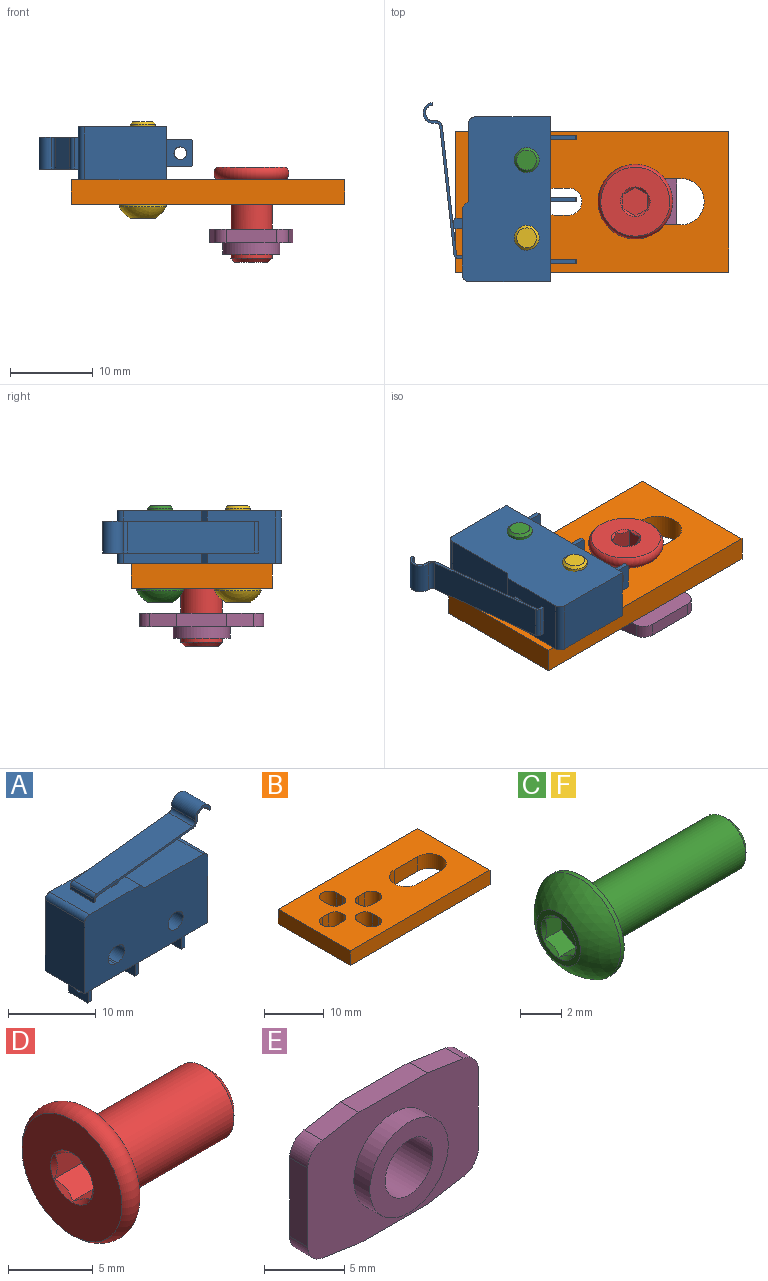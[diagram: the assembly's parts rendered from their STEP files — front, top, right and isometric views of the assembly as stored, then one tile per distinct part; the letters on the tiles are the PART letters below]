
ASSEMBLY  parts=6 mates=5
PART A: 58 faces, bbox 21.6x6.4x18.6 mm
  f0: cylinder r=0.76mm len=1.52mm, axis (-1,0,0), area 2.4mm2, adj f51,f52
  f1: cylinder r=0.76mm len=1.52mm, axis (-1,0,0), area 2.4mm2, adj f44,f45
  f2: cylinder r=0.76mm len=1.52mm, axis (-1,0,0), area 2.4mm2, adj f37,f38
  f3: cylinder r=1.21mm len=6.35mm, axis (0,1,0), area 24.1mm2, adj f26,f27,f34,f36
  f4: cylinder r=1.21mm len=6.35mm, axis (0,1,0), area 48.1mm2, adj f26,f27
  f5: cylinder r=1.27mm len=3.81mm, axis (0,1,0), area 15.2mm2, adj f14,f15,f22,f23
  f6: cylinder r=0.97mm len=3.81mm, axis (0,1,0), area 11.6mm2, adj f14,f21,f22,f23
  f7: cylinder r=1.02mm len=2.21mm, axis (0,1,0), area 1.4mm2, adj f9,f10,f11,f13
  f8: cylinder r=1.02mm len=2.21mm, axis (0,1,0), area 0.9mm2, adj f9,f10,f12,f13
  f9: plane 1.27x1.13mm, normal (0,-1,0), area 1.3mm2, adj f7,f8,f11,f12,f13,f24
  f10: plane 1.27x1.13mm, normal (0,1,0), area 1.3mm2, adj f7,f8,f11,f12,f13,f24
  f11: plane 2.21x0.91mm, normal (1,0,0), area 2mm2, adj f7,f9,f10,f24
  f12: plane 2.21x0.91mm, normal (-1,0,0), area 2mm2, adj f8,f9,f10,f24
  f13: plane 15.38x3.81mm, normal (0.11,0,-0.99), area 58.2mm2, adj f7,f8,f9,f10,f20,f21,f22,f23
  f14: plane 3.81x0.3mm, normal (0.14,0,-0.99), area 1.2mm2, adj f5,f6,f22,f23
  f15: cylinder r=0.51mm len=3.81mm, axis (0,1,0), area 3.1mm2, adj f5,f16,f22,f23
  f16: plane 15.38x3.81mm, normal (-0.11,0,0.99), area 59mm2, adj f15,f17,f22,f23
  f17: cylinder r=0.51mm len=3.81mm, axis (0,1,0), area 2.8mm2, adj f16,f18,f22,f23
  f18: plane 3.81x0.51mm, normal (-1,0,0), area 1.9mm2, adj f17,f22,f23,f24
  f19: plane 3.81x0.51mm, normal (1,0,0), area 1.9mm2, adj f20,f22,f23,f24
  f20: cylinder r=0.2mm len=3.81mm, axis (0,1,0), area 1.1mm2, adj f13,f19,f22,f23
  f21: cylinder r=0.81mm len=3.81mm, axis (0,1,0), area 5mm2, adj f6,f13,f22,f23
  f22: plane 18.8x4.75mm, normal (0,-1,0), area 6.4mm2, adj f5,f6,f13,f14,f15,f16,f17,f18
  f23: plane 18.8x4.75mm, normal (0,1,0), area 6.4mm2, adj f5,f6,f13,f14,f15,f16,f17,f18
  f24: plane 8.18x6.35mm, normal (0,0,1), area 48mm2, adj f9,f10,f11,f12,f18,f19,f22,f23
  f25: plane 19.84x6.35mm, normal (0,0,-1), area 120.9mm2, adj f26,f27,f28,f33,f37,f38,f39,f43
  f26: plane 19.84x10.62mm, normal (0,-1,0), area 193.1mm2, adj f3,f4,f24,f25,f28,f29,f30,f31
  f27: plane 19.84x10.62mm, normal (0,1,0), area 193.1mm2, adj f3,f4,f24,f25,f28,f29,f30,f31
  f28: plane 9.14x6.35mm, normal (1,0,0), area 58.1mm2, adj f25,f26,f27,f29
  f29: cylinder r=0.76mm len=6.35mm, axis (0,1,0), area 7.6mm2, adj f26,f27,f28,f30
  f30: plane 9.42x6.35mm, normal (0,0,1), area 59.8mm2, adj f26,f27,f29,f31
  f31: plane 6.35x0.71mm, normal (0.71,0,0.71), area 6.4mm2, adj f24,f26,f27,f30
  f32: cylinder r=0.76mm len=6.35mm, axis (0,1,0), area 7.6mm2, adj f24,f26,f27,f33
  f33: plane 9.86x6.35mm, normal (-1,0,0), area 62.6mm2, adj f25,f26,f27,f32
  f34: plane 6.35x0.25mm, normal (0,0,1), area 1.6mm2, adj f3,f26,f27,f35
  f35: cylinder r=1.21mm len=6.35mm, axis (0,1,0), area 24.1mm2, adj f26,f27,f34,f36
  f36: plane 6.35x0.25mm, normal (0,0,-1), area 1.6mm2, adj f3,f26,f27,f35
  f37: plane 3.3x3.2mm, normal (1,0,0), area 8.7mm2, adj f2,f25,f39,f40,f41,f42,f43
  f38: plane 3.3x3.2mm, normal (-1,0,0), area 8.7mm2, adj f2,f25,f39,f40,f41,f42,f43
  f39: plane 3.07x0.51mm, normal (0,-1,0), area 1.6mm2, adj f25,f37,f38,f40
  f40: plane 0.51x0.13mm, normal (0,-0.71,-0.71), area 0.1mm2, adj f37,f38,f39,f41
  f41: plane 3.05x0.51mm, normal (0,0,-1), area 1.5mm2, adj f37,f38,f40,f42
  f42: plane 0.51x0.13mm, normal (0,0.71,-0.71), area 0.1mm2, adj f37,f38,f41,f43
  f43: plane 3.07x0.51mm, normal (0,1,0), area 1.6mm2, adj f25,f37,f38,f42
  f44: plane 3.3x3.2mm, normal (1,0,0), area 8.7mm2, adj f1,f25,f46,f47,f48,f49,f50
  f45: plane 3.3x3.2mm, normal (-1,0,0), area 8.7mm2, adj f1,f25,f46,f47,f48,f49,f50
  f46: plane 3.07x0.51mm, normal (0,-1,0), area 1.6mm2, adj f25,f44,f45,f47
  f47: plane 0.51x0.13mm, normal (0,-0.71,-0.71), area 0.1mm2, adj f44,f45,f46,f48
  f48: plane 3.05x0.51mm, normal (0,0,-1), area 1.5mm2, adj f44,f45,f47,f49
  f49: plane 0.51x0.13mm, normal (0,0.71,-0.71), area 0.1mm2, adj f44,f45,f48,f50
  f50: plane 3.07x0.51mm, normal (0,1,0), area 1.6mm2, adj f25,f44,f45,f49
  f51: plane 3.3x3.2mm, normal (1,0,0), area 8.7mm2, adj f0,f25,f53,f54,f55,f56,f57
  f52: plane 3.3x3.2mm, normal (-1,0,0), area 8.7mm2, adj f0,f25,f53,f54,f55,f56,f57
  f53: plane 3.07x0.51mm, normal (0,-1,0), area 1.6mm2, adj f25,f51,f52,f54
  f54: plane 0.51x0.13mm, normal (0,-0.71,-0.71), area 0.1mm2, adj f51,f52,f53,f55
  f55: plane 3.05x0.51mm, normal (0,0,-1), area 1.5mm2, adj f51,f52,f54,f56
  f56: plane 0.51x0.13mm, normal (0,0.71,-0.71), area 0.1mm2, adj f51,f52,f55,f57
  f57: plane 3.07x0.51mm, normal (0,1,0), area 1.6mm2, adj f25,f51,f52,f56
PART B: 26 faces, bbox 33x17x3 mm
  f0: cylinder r=1.65mm len=3.3mm, axis (0,0,1), area 15.6mm2, adj f6,f7,f24,f25
  f1: cylinder r=1.65mm len=3.3mm, axis (0,0,1), area 15.6mm2, adj f6,f7,f12,f14
  f2: plane 17x3mm, normal (-1,0,0), area 51mm2, adj f3,f5,f6,f7
  f3: plane 33x3mm, normal (0,-1,0), area 99mm2, adj f2,f4,f6,f7
  f4: plane 17x3mm, normal (1,0,0), area 51mm2, adj f3,f5,f6,f7
  f5: plane 33x3mm, normal (0,1,0), area 99mm2, adj f2,f4,f6,f7
  f6: plane 33x17mm, normal (0,0,1), area 451.6mm2, adj f0,f1,f2,f3,f4,f5,f8,f9
  f7: plane 33x17mm, normal (0,0,-1), area 451.6mm2, adj f0,f1,f2,f3,f4,f5,f8,f9
  f8: cylinder r=2.8mm len=5.6mm, axis (0,0,1), area 26.4mm2, adj f6,f7,f9,f11
  f9: plane 5.5x3mm, normal (0,-1,0), area 16.5mm2, adj f6,f7,f8,f10
  f10: cylinder r=2.8mm len=5.6mm, axis (0,0,1), area 26.4mm2, adj f6,f7,f9,f11
  f11: plane 5.5x3mm, normal (0,1,0), area 16.5mm2, adj f6,f7,f8,f10
  f12: plane 3x1.5mm, normal (1,0,0), area 4.5mm2, adj f1,f6,f7,f13
  f13: cylinder r=1.65mm len=3.3mm, axis (0,0,1), area 15.6mm2, adj f6,f7,f12,f14
  f14: plane 3x1.5mm, normal (-1,0,0), area 4.5mm2, adj f1,f6,f7,f13
  f15: cylinder r=1.65mm len=3.3mm, axis (0,0,1), area 15.6mm2, adj f6,f7,f16,f18
  f16: plane 3x1.5mm, normal (0,-1,0), area 4.5mm2, adj f6,f7,f15,f17
  f17: cylinder r=1.65mm len=3.3mm, axis (0,0,1), area 15.6mm2, adj f6,f7,f16,f18
  f18: plane 3x1.5mm, normal (0,1,0), area 4.5mm2, adj f6,f7,f15,f17
  f19: cylinder r=1.65mm len=3.3mm, axis (0,0,1), area 15.6mm2, adj f6,f7,f20,f22
  f20: plane 3x1.5mm, normal (0,1,0), area 4.5mm2, adj f6,f7,f19,f21
  f21: cylinder r=1.65mm len=3.3mm, axis (0,0,1), area 15.6mm2, adj f6,f7,f20,f22
  f22: plane 3x1.5mm, normal (0,-1,0), area 4.5mm2, adj f6,f7,f19,f21
  f23: cylinder r=1.65mm len=3.3mm, axis (0,0,1), area 15.6mm2, adj f6,f7,f24,f25
  f24: plane 3x1.5mm, normal (-1,0,0), area 4.5mm2, adj f0,f6,f7,f23
  f25: plane 3x1.5mm, normal (1,0,0), area 4.5mm2, adj f0,f6,f7,f23
PART C: 15 faces, bbox 12x5.7x5.7 mm
  f0: cone r=1.2mm half-angle=45deg, axis (-1,0,0), area 1.5mm2, adj f6,f9,f10,f11,f12,f13,f14
  f1: cylinder r=2.85mm len=5.7mm, axis (1,0,0), area 4.5mm2, adj f2,f7
  f2: sphere r=3.17mm, area 27.9mm2, adj f1,f6
  f3: cone r=1.2mm half-angle=45deg, axis (-1,0,0), area 3.6mm2, adj f4,f5
  f4: cylinder r=1.5mm len=9.7mm, axis (1,0,0), area 91.4mm2, adj f3,f7
  f5: plane 2.4x2.4mm, normal (1,0,0), area 4.5mm2, adj f3
  f6: plane 3x3mm, normal (-1,0,0), area 2.5mm2, adj f0,f2
  f7: plane 5.7x5.7mm, normal (1,0,0), area 18.4mm2, adj f1,f4
  f8: plane 2.31x2mm, normal (-1,0,0), area 3.5mm2, adj f9,f10,f11,f12,f13,f14
  f9: plane 1.15x1mm, normal (0,-0.5,-0.87), area 1.2mm2, adj f0,f8,f10,f14
  f10: plane 1.16x1.15mm, normal (0,-1,0), area 1.2mm2, adj f0,f8,f9,f11
  f11: plane 1.15x1mm, normal (0,-0.5,0.87), area 1.2mm2, adj f0,f8,f10,f12
  f12: plane 1.15x1mm, normal (0,0.5,0.87), area 1.2mm2, adj f0,f8,f11,f13
  f13: plane 1.16x1.15mm, normal (0,1,0), area 1.2mm2, adj f0,f8,f12,f14
  f14: plane 1.15x1mm, normal (0,0.5,-0.87), area 1.2mm2, adj f0,f8,f9,f13
PART D: 14 faces, bbox 11.8x9.7x9.7 mm
  f0: cone r=1.78mm half-angle=45deg, axis (-1,0,0), area 3.1mm2, adj f5,f8,f9,f10,f11,f12,f13
  f1: torus R=3.5mm, axis (1,0,0), area 46.7mm2, adj f5,f6
  f2: cone r=2mm half-angle=45deg, axis (-1,0,0), area 10mm2, adj f3,f4
  f3: cylinder r=2.5mm len=9.5mm, axis (1,0,0), area 149.2mm2, adj f2,f6
  f4: plane 4x4mm, normal (1,0,0), area 12.6mm2, adj f2
  f5: plane 8.32x8.32mm, normal (-1,0,0), area 44.4mm2, adj f0,f1
  f6: plane 8.32x8.32mm, normal (1,0,0), area 34.8mm2, adj f1,f3
  f7: plane 3.46x3mm, normal (-1,0,0), area 7.8mm2, adj f8,f9,f10,f11,f12,f13
  f8: plane 2.25x1.5mm, normal (0,-0.5,-0.87), area 3.6mm2, adj f0,f7,f9,f13
  f9: plane 2.25x1.73mm, normal (0,-1,0), area 3.6mm2, adj f0,f7,f8,f10
  f10: plane 2.25x1.5mm, normal (0,-0.5,0.87), area 3.6mm2, adj f0,f7,f9,f11
  f11: plane 2.25x1.5mm, normal (0,0.5,0.87), area 3.6mm2, adj f0,f7,f10,f12
  f12: plane 2.25x1.73mm, normal (0,1,0), area 3.6mm2, adj f0,f7,f11,f13
  f13: plane 2.25x1.5mm, normal (0,0.5,-0.87), area 3.6mm2, adj f0,f7,f8,f12
PART E: 17 faces, bbox 15x3x10 mm
  f0: cylinder r=2.1mm len=4.2mm, axis (0,-1,0), area 39.6mm2, adj f15,f16
  f1: cylinder r=3.45mm len=6.9mm, axis (0,1,0), area 30.3mm2, adj f2,f16
  f2: plane 15x10mm, normal (0,-1,0), area 104.8mm2, adj f1,f3,f4,f5,f6,f7,f8,f9
  f3: cylinder r=1.5mm len=1.6mm, axis (0,1,0), area 3.4mm2, adj f2,f4,f14,f15
  f4: plane 3.24x1.6mm, normal (0.16,0,0.99), area 5.2mm2, adj f2,f3,f5,f15
  f5: plane 6x1.6mm, normal (0,0,1), area 9.6mm2, adj f2,f4,f6,f15
  f6: plane 3.24x1.6mm, normal (-0.16,0,0.99), area 5.2mm2, adj f2,f5,f7,f15
  f7: cylinder r=1.5mm len=1.6mm, axis (0,1,0), area 3.4mm2, adj f2,f6,f8,f15
  f8: plane 6x1.6mm, normal (-1,0,0), area 9.6mm2, adj f2,f7,f9,f15
  f9: cylinder r=1.5mm len=1.6mm, axis (0,1,0), area 3.4mm2, adj f2,f8,f10,f15
  f10: plane 3.24x1.6mm, normal (-0.16,0,-0.99), area 5.2mm2, adj f2,f9,f11,f15
  f11: plane 6x1.6mm, normal (0,0,-1), area 9.6mm2, adj f2,f10,f12,f15
  f12: plane 3.24x1.6mm, normal (0.16,0,-0.99), area 5.2mm2, adj f2,f11,f13,f15
  f13: cylinder r=1.5mm len=1.6mm, axis (0,1,0), area 3.4mm2, adj f2,f12,f14,f15
  f14: plane 6x1.6mm, normal (1,0,0), area 9.6mm2, adj f2,f3,f13,f15
  f15: plane 15x10mm, normal (0,1,0), area 128.3mm2, adj f0,f3,f4,f5,f6,f7,f8,f9
  f16: plane 6.9x6.9mm, normal (0,-1,0), area 23.5mm2, adj f0,f1
PART F: same geometry as C
PLACE A rot(axis=(-0.58,-0.58,0.58),120deg) t=(11.46,8.79,6.18)mm
PLACE B at identity fixed
PLACE C rot(axis=(-0.58,-0.58,-0.58),120deg) t=(8.6,13.5,6)mm
PLACE D rot(axis=(0.58,0.58,-0.58),120deg) t=(21.7,8.5,-5)mm
PLACE E rot(axis=(0.58,-0.58,-0.58),120deg) t=(21.7,8.5,-3)mm
PLACE F rot(axis=(-0.58,-0.58,-0.58),120deg) t=(8.6,4.13,6)mm
MATE planar F.f1 <-> B.f7  axis (0,0,1) through (8.6,4.13,0)mm
MATE revolute C.f1 <-> B.f13  axis (0,0,1) through (8.6,13.5,0)mm
MATE revolute E.f0 <-> B.f8  axis (0,0,1) through (21.7,8.5,-3)mm
MATE fastened A.f4 <-> B.f13  axis (0,0,-1) through (8.6,13.5,3)mm
MATE revolute D.f0 <-> B.f8  axis (0,0,-1) through (21.7,8.5,3)mm
